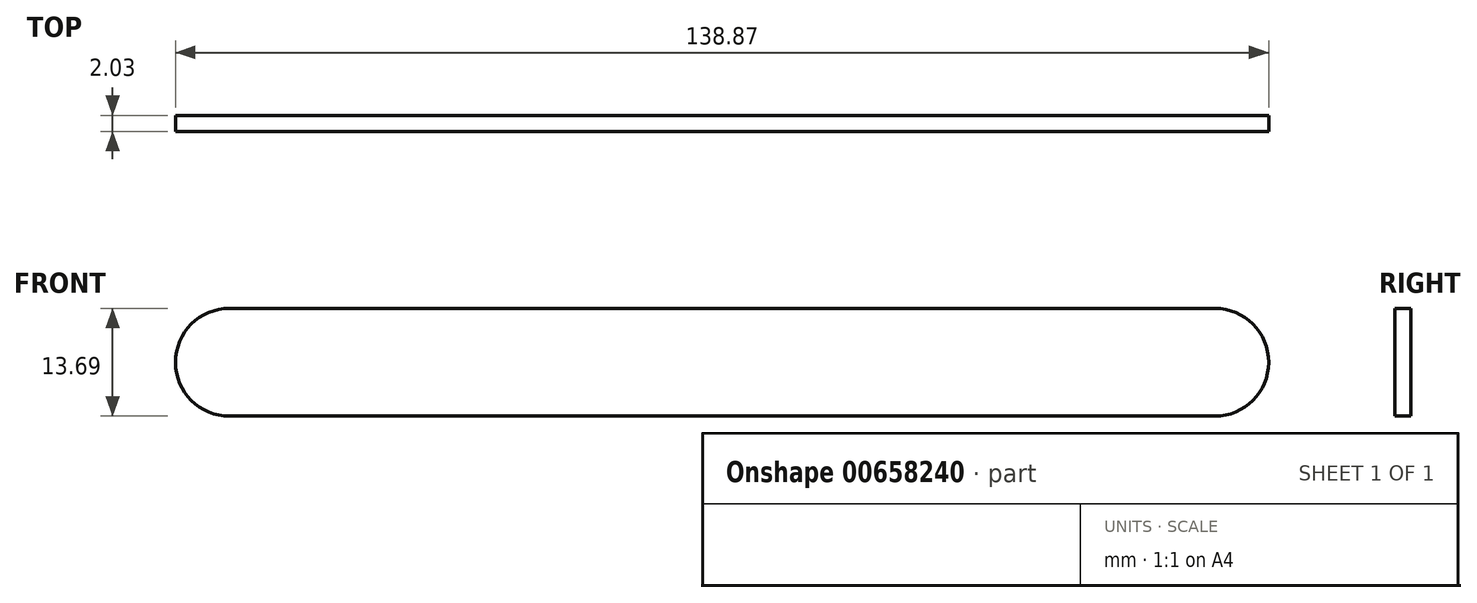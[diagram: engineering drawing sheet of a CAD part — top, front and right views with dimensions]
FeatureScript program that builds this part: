
annotation { "Feature Type Name" : "Feature", "Feature Type Description" : "" }
export const myFeature = defineFeature(function(context is Context, id is Id, definition is map)
    precondition{}
    {
        {
            var Q0;
            Q0=qCreatedBy(makeId("Front.planeOp"),FACE);
            var sketch = newSketch(context, id + "F0", { "sketchPlane" : qUnion([Q0])});
            skLineSegment(sketch, "E0.bottom", {"start": v(-106.13, 24.56) * mm, "end": v(19.04, 24.56) * mm});
            skLineSegment(sketch, "E0.top", {"start": v(-106.13, 10.87) * mm, "end": v(19.04, 10.87) * mm});
            skLineSegment(sketch, "E0.left", {"start": v(-106.13, 24.56) * mm, "end": v(-106.13, 10.87) * mm});
            skLineSegment(sketch, "E0.right", {"start": v(19.04, 24.56) * mm, "end": v(19.04, 10.87) * mm});
            skArc(sketch, "E1", {"start": v(-106.13, 24.56) * mm, "mid": v(-112.98, 17.71) * mm, "end": v(-106.13, 10.87) * mm});
            skArc(sketch, "E2", {"start": v(19.04, 10.87) * mm, "mid": v(25.89, 17.71) * mm, "end": v(19.04, 24.56) * mm});
            skSolve(sketch);
        }
        {
            var Q0;
            Q0=makeQuery(id+"F0.imprint","IMPRINT",FACE,{"disambiguationData":[TD([[makeQuery(id+"F0.imprint","IMPRINT",EDGE,{"derivedFrom":sQuery(id+"F0.wireOp",EDGE,"E0.bottom")}),-1.0]])]});
            var Q1;
            Q1=makeQuery(id+"F0.imprint","IMPRINT",FACE,{"disambiguationData":[TD([[makeQuery(id+"F0.imprint","IMPRINT",EDGE,{"derivedFrom":sQuery(id+"F0.wireOp",EDGE,"E0.left")}),-1.0]])]});
            var Q2;
            Q2=makeQuery(id+"F0.imprint","IMPRINT",FACE,{"disambiguationData":[TD([[makeQuery(id+"F0.imprint","IMPRINT",EDGE,{"derivedFrom":sQuery(id+"F0.wireOp",EDGE,"E0.right")}),1.0]])]});
            extrude(context, id + "F1", {"entities" : qUnion([Q0, Q1, Q2]), "depth" : 2.03 * mm, "offsetDistance" : 25.4 * mm});
        }
    });
